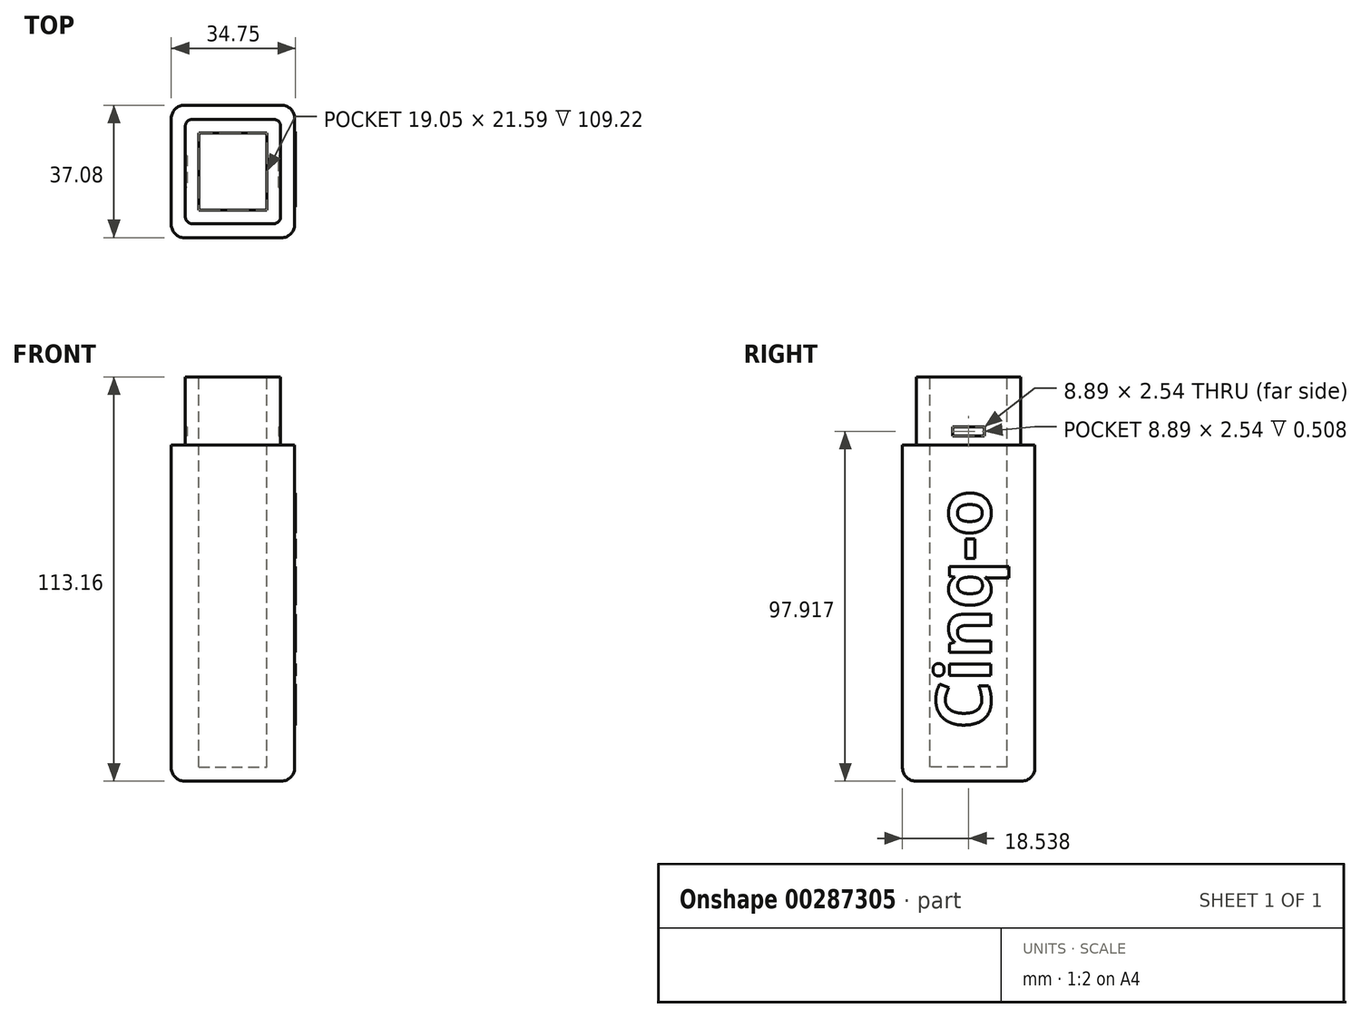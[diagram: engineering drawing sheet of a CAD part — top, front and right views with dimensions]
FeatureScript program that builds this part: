
annotation { "Feature Type Name" : "Feature", "Feature Type Description" : "" }
export const myFeature = defineFeature(function(context is Context, id is Id, definition is map)
    precondition{}
    {
        {
            var Q0;
            Q0=qCreatedBy(makeId("Top.planeOp"),FACE);
            var sketch = newSketch(context, id + "F0", { "sketchPlane" : qUnion([Q0])});
            skLineSegment(sketch, "E0.bottom", {"start": v(0, 0) * mm, "end": v(34.54, 0) * mm});
            skLineSegment(sketch, "E0.top", {"start": v(0, -37.08) * mm, "end": v(34.54, -37.08) * mm});
            skLineSegment(sketch, "E0.left", {"start": v(0, 0) * mm, "end": v(0, -37.08) * mm});
            skLineSegment(sketch, "E0.right", {"start": v(34.54, 0) * mm, "end": v(34.54, -37.08) * mm});
            skSolve(sketch);
        }
        {
            var Q0;
            Q0 = qSketchRegion(id + "F0", true);
            extrude(context, id + "F1", {"entities" : qUnion([Q0]), "depth" : 94.1 * mm});
        }
        {
            var Q0;
            Q0=makeQuery(id+"F1.opExtrude","CAP_FACE",FACE,{"disambiguationData":[OSD([sQuery(id+"F0.wireOp",EDGE,"E0.bottom"),sQuery(id+"F0.wireOp",EDGE,"E0.top"),sQuery(id+"F0.wireOp",EDGE,"E0.left"),sQuery(id+"F0.wireOp",EDGE,"E0.right")])],"isStart":false});
            var sketch = newSketch(context, id + "F2", { "sketchPlane" : qUnion([Q0])});
            skLineSegment(sketch, "E1.bottom", {"start": v(3.94, -3.94) * mm, "end": v(30.6, -3.94) * mm});
            skLineSegment(sketch, "E1.top", {"start": v(3.94, -33.15) * mm, "end": v(30.6, -33.15) * mm});
            skLineSegment(sketch, "E1.left", {"start": v(3.94, -3.94) * mm, "end": v(3.94, -33.15) * mm});
            skLineSegment(sketch, "E1.right", {"start": v(30.6, -3.94) * mm, "end": v(30.6, -33.15) * mm});
            skSolve(sketch);
        }
        {
            var Q0;
            Q0 = qSketchRegion(id + "F2", true);
            extrude(context, id + "F3", {"entities" : qUnion([Q0]), "operationType" : NewBodyOperationType.ADD, "depth" : 19.05 * mm});
        }
        {
            var Q0;
            Q0=makeQuery(id+"F3.opExtrude","CAP_FACE",FACE,{"disambiguationData":[OSD([sQuery(id+"F2.wireOp",EDGE,"E1.bottom"),sQuery(id+"F2.wireOp",EDGE,"E1.top"),sQuery(id+"F2.wireOp",EDGE,"E1.left"),sQuery(id+"F2.wireOp",EDGE,"E1.right")])],"isStart":false});
            var sketch = newSketch(context, id + "F4", { "sketchPlane" : qUnion([Q0])});
            skLineSegment(sketch, "E2.bottom", {"start": v(7.75, -7.75) * mm, "end": v(26.8, -7.75) * mm});
            skLineSegment(sketch, "E2.top", {"start": v(7.75, -29.34) * mm, "end": v(26.8, -29.34) * mm});
            skLineSegment(sketch, "E2.left", {"start": v(7.75, -7.75) * mm, "end": v(7.75, -29.34) * mm});
            skLineSegment(sketch, "E2.right", {"start": v(26.8, -7.75) * mm, "end": v(26.8, -29.34) * mm});
            skSolve(sketch);
        }
        {
            var Q0;
            Q0 = qSketchRegion(id + "F4", true);
            extrude(context, id + "F5", {"entities" : qUnion([Q0]), "operationType" : NewBodyOperationType.REMOVE, "oppositeDirection" : true, "depth" : 109.22 * mm});
        }
        {
            var Q0;
            Q0=makeQuery(id+"F1.opExtrude","SWEPT_EDGE",EDGE,{"disambiguationData":[OSD([sQuery(id+"F0.wireOp",EDGE,"E0.bottom"),sQuery(id+"F0.wireOp",EDGE,"E0.right")])]});
            var Q1;
            Q1=makeQuery(id+"F1.opExtrude","SWEPT_EDGE",EDGE,{"disambiguationData":[OSD([sQuery(id+"F0.wireOp",EDGE,"E0.bottom"),sQuery(id+"F0.wireOp",EDGE,"E0.left")])]});
            var Q2;
            Q2=makeQuery(id+"F1.opExtrude","SWEPT_EDGE",EDGE,{"disambiguationData":[OSD([sQuery(id+"F0.wireOp",EDGE,"E0.top"),sQuery(id+"F0.wireOp",EDGE,"E0.right")])]});
            var Q3;
            Q3=makeQuery(id+"F1.opExtrude","CAP_EDGE",EDGE,{"disambiguationData":[OSD([sQuery(id+"F0.wireOp",EDGE,"E0.right")])],"isStart":true});
            var Q4;
            Q4=makeQuery(id+"F1.opExtrude","CAP_EDGE",EDGE,{"disambiguationData":[OSD([sQuery(id+"F0.wireOp",EDGE,"E0.bottom")])],"isStart":true});
            var Q5;
            Q5=makeQuery(id+"F1.opExtrude","SWEPT_EDGE",EDGE,{"disambiguationData":[OSD([sQuery(id+"F0.wireOp",EDGE,"E0.top"),sQuery(id+"F0.wireOp",EDGE,"E0.left")])]});
            var Q6;
            Q6=makeQuery(id+"F1.opExtrude","CAP_EDGE",EDGE,{"disambiguationData":[OSD([sQuery(id+"F0.wireOp",EDGE,"E0.left")])],"isStart":true});
            var Q7;
            Q7=makeQuery(id+"F1.opExtrude","CAP_EDGE",EDGE,{"disambiguationData":[OSD([sQuery(id+"F0.wireOp",EDGE,"E0.top")])],"isStart":true});
            fillet(context, id + "F6", {"entities" : qUnion([Q0, Q1, Q2, Q3, Q4, Q5, Q6, Q7]), "radius" : 3.68 * mm, "tangentPropagation" : true, "allowEdgeOverflow" : false});
        }
        {
            var Q0;
            Q0=makeQuery(id+"F3.opExtrude","SWEPT_EDGE",EDGE,{"disambiguationData":[OSD([sQuery(id+"F2.wireOp",EDGE,"E1.bottom"),sQuery(id+"F2.wireOp",EDGE,"E1.right")])]});
            var Q1;
            Q1=makeQuery(id+"F3.opExtrude","SWEPT_EDGE",EDGE,{"disambiguationData":[OSD([sQuery(id+"F2.wireOp",EDGE,"E1.top"),sQuery(id+"F2.wireOp",EDGE,"E1.right")])]});
            var Q2;
            Q2=makeQuery(id+"F3.opExtrude","SWEPT_EDGE",EDGE,{"disambiguationData":[OSD([sQuery(id+"F2.wireOp",EDGE,"E1.bottom"),sQuery(id+"F2.wireOp",EDGE,"E1.left")])]});
            var Q3;
            Q3=makeQuery(id+"F3.opExtrude","SWEPT_EDGE",EDGE,{"disambiguationData":[OSD([sQuery(id+"F2.wireOp",EDGE,"E1.top"),sQuery(id+"F2.wireOp",EDGE,"E1.left")])]});
            fillet(context, id + "F7", {"entities" : qUnion([Q0, Q1, Q2, Q3]), "radius" : 1.9 * mm, "tangentPropagation" : true, "allowEdgeOverflow" : false});
        }
        {
            var Q0;
            Q0=makeQuery(id+"F1.opExtrude","SWEPT_FACE",FACE,{"disambiguationData":[OSD([sQuery(id+"F0.wireOp",EDGE,"E0.right")])]});
            var sketch = newSketch(context, id + "F8", { "sketchPlane" : qUnion([Q0])});
            skText(sketch, "E3", { "text": "Cinq-o", "fontName": "OpenSans-Bold.ttf"});
            const initialGuessF8  = {"E3": [-0.01243, 0.01444, 0, 1, 0.01524]};
            skSetInitialGuess(sketch, initialGuessF8);
            skSolve(sketch);
        }
        {
            var Q0;
            Q0 = qSketchRegion(id + "F8", true);
            extrude(context, id + "F9", {"entities" : qUnion([Q0]), "operationType" : NewBodyOperationType.ADD, "depth" : 0.2 * mm});
        }
        {
            var Q0;
            Q0=makeQuery(id+"F3.opExtrude","SWEPT_FACE",FACE,{"disambiguationData":[OSD([sQuery(id+"F2.wireOp",EDGE,"E1.right")])]});
            var sketch = newSketch(context, id + "F10", { "sketchPlane" : qUnion([Q0])});
            skLineSegment(sketch, "E4.bottom", {"start": v(-22.99, 99.19) * mm, "end": v(-14.1, 99.19) * mm});
            skLineSegment(sketch, "E4.top", {"start": v(-22.99, 96.65) * mm, "end": v(-14.1, 96.65) * mm});
            skLineSegment(sketch, "E4.left", {"start": v(-22.99, 99.19) * mm, "end": v(-22.99, 96.65) * mm});
            skLineSegment(sketch, "E4.right", {"start": v(-14.1, 99.19) * mm, "end": v(-14.1, 96.65) * mm});
            skSolve(sketch);
        }
        {
            var Q0;
            Q0 = qSketchRegion(id + "F10", true);
            extrude(context, id + "F11", {"entities" : qUnion([Q0]), "operationType" : NewBodyOperationType.REMOVE, "oppositeDirection" : true, "depth" : 0.5 * mm});
        }
        {
            var Q0;
            Q0=makeQuery(id+"F3.opExtrude","SWEPT_FACE",FACE,{"disambiguationData":[OSD([sQuery(id+"F2.wireOp",EDGE,"E1.left")])]});
            var sketch = newSketch(context, id + "F12", { "sketchPlane" : qUnion([Q0])});
            skLineSegment(sketch, "E5.bottom", {"start": v(14.1, 99.19) * mm, "end": v(22.99, 99.19) * mm});
            skLineSegment(sketch, "E5.top", {"start": v(14.1, 96.65) * mm, "end": v(22.99, 96.65) * mm});
            skLineSegment(sketch, "E5.left", {"start": v(14.1, 99.19) * mm, "end": v(14.1, 96.65) * mm});
            skLineSegment(sketch, "E5.right", {"start": v(22.99, 99.19) * mm, "end": v(22.99, 96.65) * mm});
            skSolve(sketch);
        }
        {
            var Q0;
            Q0 = qSketchRegion(id + "F12", true);
            extrude(context, id + "F13", {"entities" : qUnion([Q0]), "operationType" : NewBodyOperationType.REMOVE, "oppositeDirection" : true, "depth" : 0.5 * mm});
        }
        {
            var Q0;
            Q0=makeQuery(id+"F3.opExtrude","SWEPT_FACE",FACE,{"disambiguationData":[OSD([sQuery(id+"F2.wireOp",EDGE,"E1.bottom")])]});
            var sketch = newSketch(context, id + "F14", { "sketchPlane" : qUnion([Q0])});
            skLineSegment(sketch, "E6.bottom", {"start": v(-20.45, 99.19) * mm, "end": v(-14.1, 99.19) * mm});
            skLineSegment(sketch, "E6.top", {"start": v(-20.45, 96.65) * mm, "end": v(-14.1, 96.65) * mm});
            skLineSegment(sketch, "E6.left", {"start": v(-20.45, 99.19) * mm, "end": v(-20.45, 96.65) * mm});
            skLineSegment(sketch, "E6.right", {"start": v(-14.1, 99.19) * mm, "end": v(-14.1, 96.65) * mm});
            skSolve(sketch);
        }
        {
            var Q0;
            Q0=makeQuery(id+"F3.opExtrude","SWEPT_FACE",FACE,{"disambiguationData":[OSD([sQuery(id+"F2.wireOp",EDGE,"E1.top")])]});
            var sketch = newSketch(context, id + "F15", { "sketchPlane" : qUnion([Q0])});
            skLineSegment(sketch, "E7.bottom", {"start": v(14.1, 99.19) * mm, "end": v(20.45, 99.19) * mm});
            skLineSegment(sketch, "E7.top", {"start": v(14.1, 96.65) * mm, "end": v(20.45, 96.65) * mm});
            skLineSegment(sketch, "E7.left", {"start": v(14.1, 99.19) * mm, "end": v(14.1, 96.65) * mm});
            skLineSegment(sketch, "E7.right", {"start": v(20.45, 99.19) * mm, "end": v(20.45, 96.65) * mm});
            skSolve(sketch);
        }
        {
            var Q0;
            Q0=makeQuery(id+"F1.opExtrude","SWEPT_BODY",BODY,{"disambiguationData":[OSD([sQuery(id+"F0.wireOp",EDGE,"E0.bottom"),sQuery(id+"F0.wireOp",EDGE,"E0.top"),sQuery(id+"F0.wireOp",EDGE,"E0.left"),sQuery(id+"F0.wireOp",EDGE,"E0.right")])]});
            transform(context, id + "F16", {"entities" : qUnion([Q0]), "transformType" : TransformType.TRANSLATION_3D, "dx" : 50.8 * mm, "dy" : 0 * mm, "dz" : 0 * mm, "makeCopy" : true});
        }
        {
            var Q0;
            Q0=makeQuery(id+"F16.opPattern","COPY",BODY,{"derivedFrom":makeQuery(id+"F1.opExtrude","SWEPT_BODY",BODY,{"disambiguationData":[OSD([sQuery(id+"F0.wireOp",EDGE,"E0.bottom"),sQuery(id+"F0.wireOp",EDGE,"E0.top"),sQuery(id+"F0.wireOp",EDGE,"E0.left"),sQuery(id+"F0.wireOp",EDGE,"E0.right")])]}),"instanceName":"1"});
            deleteBodies(context, id + "F17", {"entities" : qUnion([Q0])});
        }
    });
